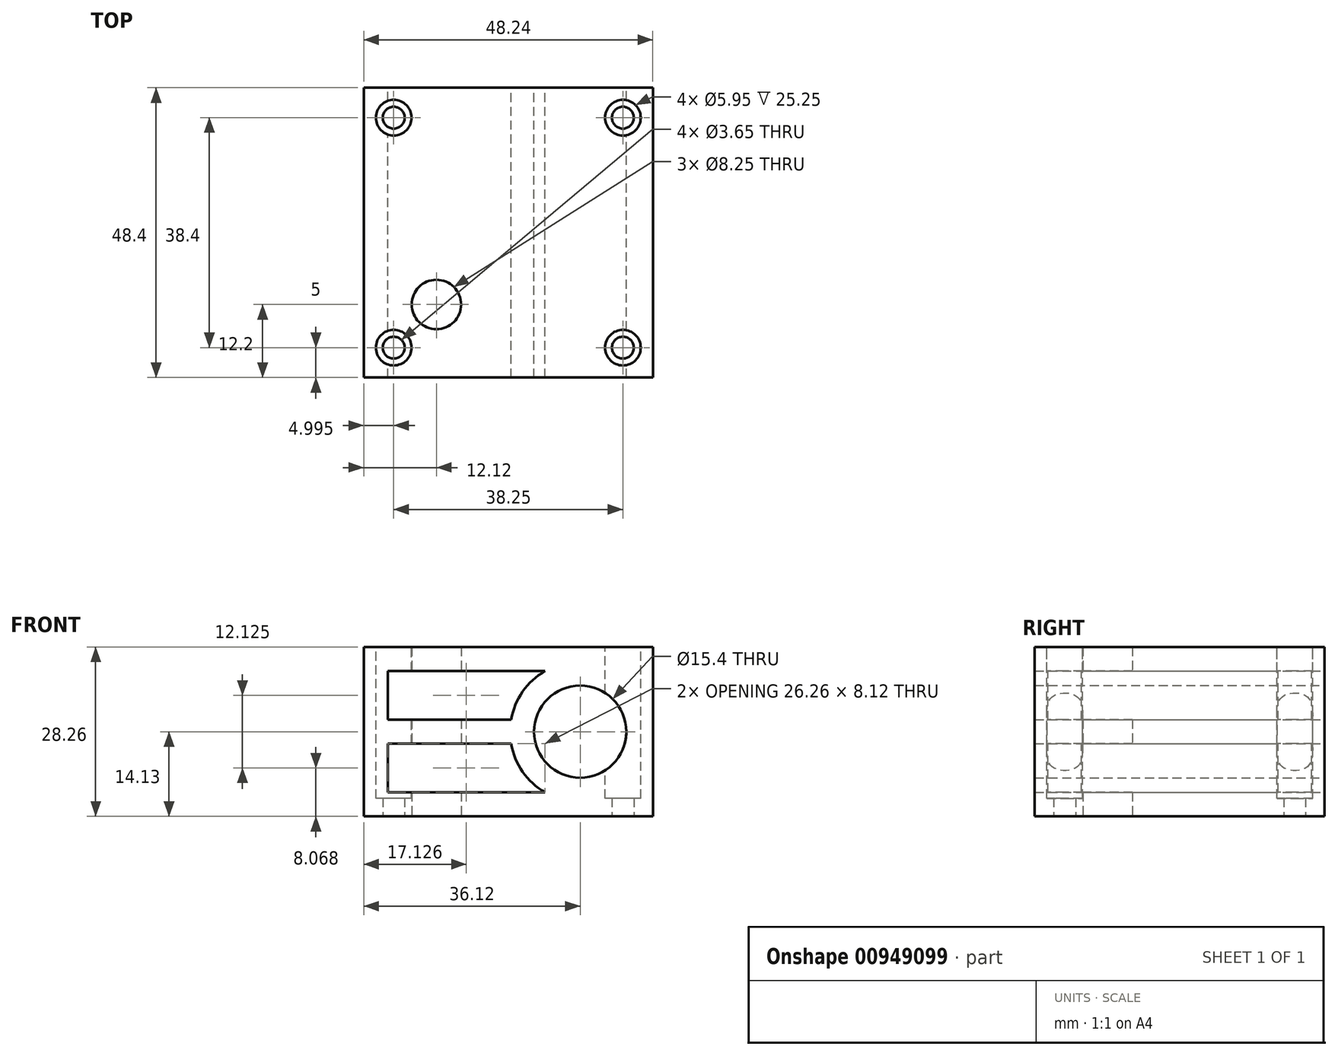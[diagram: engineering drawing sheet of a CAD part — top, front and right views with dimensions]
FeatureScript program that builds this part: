
annotation { "Feature Type Name" : "Feature", "Feature Type Description" : "" }
export const myFeature = defineFeature(function(context is Context, id is Id, definition is map)
    precondition{}
    {
        {
            assignVariable(context, id + "F0", {"name" : "tolerance_xy", "anyValue" : 0.25});
        }
        {
            assignVariable(context, id + "F1", {"name" : "tolerance_z", "anyValue" : 0.4});
        }
        {
            var Q0;
            Q0=qCreatedBy(makeId("Front.planeOp"),FACE);
            var sketch = newSketch(context, id + "F2", { "sketchPlane" : qUnion([Q0])});
            skLineSegment(sketch, "E0.bottom", {"start": v(24.12, 14.12) * mm, "end": v(-24.12, 14.12) * mm});
            skLineSegment(sketch, "E0.top", {"start": v(24.12, -14.12) * mm, "end": v(-24.12, -14.12) * mm});
            skLineSegment(sketch, "E0.left", {"start": v(24.12, 14.12) * mm, "end": v(24.12, -14.12) * mm});
            skLineSegment(sketch, "E0.right", {"start": v(-24.12, 14.12) * mm, "end": v(-24.12, -14.12) * mm});
            skPoint(sketch, "E0.middle", {"position": v(0, 0) * mm});
            skCircle(sketch, "E1", {"center": v(12, 0) * mm, "radius": 11.7 * mm});
            skCircle(sketch, "E2", {"center": v(12, 0) * mm, "radius": 7.7 * mm});
            skLineSegment(sketch, "E3.bottom", {"start": v(20.12, 10.12) * mm, "end": v(-20.12, 10.12) * mm});
            skLineSegment(sketch, "E3.top", {"start": v(20.12, -10.12) * mm, "end": v(-20.12, -10.12) * mm});
            skLineSegment(sketch, "E3.left", {"start": v(20.12, 10.12) * mm, "end": v(20.12, -10.12) * mm});
            skLineSegment(sketch, "E3.right", {"start": v(-20.12, 10.12) * mm, "end": v(-20.12, -10.12) * mm});
            skLineSegment(sketch, "E4", {"start": v(12, -10.12) * mm, "end": v(12, 10.12) * mm, "construction": true});
            skLineSegment(sketch, "E5", {"start": v(-20.12, 0) * mm, "end": v(20.12, 0) * mm, "construction": true});
            skLineSegment(sketch, "E6", {"start": v(0.47, 2) * mm, "end": v(-20.12, 2) * mm});
            skLineSegment(sketch, "E7", {"start": v(0.47, -2) * mm, "end": v(-20.12, -2) * mm});
            skLineSegment(sketch, "E8", {"start": v(10, 10.12) * mm, "end": v(10, 11.53) * mm});
            skLineSegment(sketch, "E9", {"start": v(14, 10.12) * mm, "end": v(14, 11.53) * mm});
            skLineSegment(sketch, "E10", {"start": v(10, -10.12) * mm, "end": v(10, -11.53) * mm});
            skLineSegment(sketch, "E11", {"start": v(14, -10.12) * mm, "end": v(14, -11.53) * mm});
            skLineSegment(sketch, "E12", {"start": v(23.53, 2) * mm, "end": v(20.12, 2) * mm});
            skLineSegment(sketch, "E13", {"start": v(23.53, -2) * mm, "end": v(20.12, -2) * mm});
            skSolve(sketch);
        }
        {
            var Q0;
            Q0=makeQuery(id+"F2.imprint","IMPRINT",FACE,{"disambiguationData":[TD([[makeQuery(id+"F2.imprint","IMPRINT",EDGE,{"derivedFrom":sQuery(id+"F2.wireOp",EDGE,"E0.bottom")}),1.0]])]});
            var Q1;
            {var subQ0=sQuery(id+"F2.wireOp",EDGE,"E8");Q1=makeQuery(id+"F2.imprint","IMPRINT",FACE,{"disambiguationData":[TD([[makeQuery(id+"F2.imprint","IMPRINT",EDGE,{"derivedFrom":subQ0}),-1.0]])]});}
            var Q2;
            Q2=makeQuery(id+"F2.imprint","IMPRINT",FACE,{"disambiguationData":[TD([[makeQuery(id+"F2.imprint","IMPRINT",EDGE,{"derivedFrom":sQuery(id+"F2.wireOp",EDGE,"E2")}),-1.0]])]});
            var Q3;
            {var subQ0=sQuery(id+"F2.wireOp",EDGE,"E10");Q3=makeQuery(id+"F2.imprint","IMPRINT",FACE,{"disambiguationData":[TD([[makeQuery(id+"F2.imprint","IMPRINT",EDGE,{"derivedFrom":subQ0}),1.0]])]});}
            var Q4;
            {var subQ0=sQuery(id+"F2.wireOp",EDGE,"E6");Q4=makeQuery(id+"F2.imprint","IMPRINT",FACE,{"disambiguationData":[TD([[makeQuery(id+"F2.imprint","IMPRINT",EDGE,{"derivedFrom":subQ0}),1.0]])]});}
            var Q5;
            {var subQ0=sQuery(id+"F2.wireOp",EDGE,"E12");Q5=makeQuery(id+"F2.imprint","IMPRINT",FACE,{"disambiguationData":[TD([[makeQuery(id+"F2.imprint","IMPRINT",EDGE,{"derivedFrom":subQ0}),1.0]])]});}
            var Q6;
            {var subQ0=sQuery(id+"F2.wireOp",EDGE,"E12");Q6=makeQuery(id+"F2.imprint","IMPRINT",FACE,{"disambiguationData":[TD([[makeQuery(id+"F2.imprint","IMPRINT",EDGE,{"derivedFrom":subQ0}),-1.0]])]});}
            var Q7;
            {var subQ0=sQuery(id+"F2.wireOp",EDGE,"E13");Q7=makeQuery(id+"F2.imprint","IMPRINT",FACE,{"disambiguationData":[TD([[makeQuery(id+"F2.imprint","IMPRINT",EDGE,{"derivedFrom":subQ0}),1.0]])]});}
            var Q8;
            {var subQ0=sQuery(id+"F2.wireOp",EDGE,"xwtNpsUs-C44z-uagX-IKFE-Rp0NLuXpZdO7");Q8=makeQuery(id+"F2.imprint","IMPRINT",FACE,{"disambiguationData":[TD([[makeQuery(id+"F2.imprint","IMPRINT",EDGE,{"derivedFrom":subQ0}),-1.0]])]});}
            var Q9;
            {var subQ3=sQuery(id+"F2.wireOp",EDGE,"iiPWomU2-JPy6-PKDB-MISC-S4ZnLnR1PTqr");Q9=makeQuery(id+"F2.imprint","IMPRINT",FACE,{"disambiguationData":[TD([[makeQuery(id+"F2.imprint","IMPRINT",EDGE,{"derivedFrom":subQ3}),-1.0]])]});}
            var Q10;
            {var subQ0=sQuery(id+"F2.wireOp",EDGE,"E9");Q10=makeQuery(id+"F2.imprint","IMPRINT",FACE,{"disambiguationData":[TD([[makeQuery(id+"F2.imprint","IMPRINT",EDGE,{"derivedFrom":subQ0}),-1.0]])]});}
            var Q11;
            {var subQ0=sQuery(id+"F2.wireOp",EDGE,"E8");Q11=makeQuery(id+"F2.imprint","IMPRINT",FACE,{"disambiguationData":[TD([[makeQuery(id+"F2.imprint","IMPRINT",EDGE,{"derivedFrom":subQ0}),1.0]])]});}
            var Q12;
            {var subQ0=sQuery(id+"F2.wireOp",EDGE,"E11");Q12=makeQuery(id+"F2.imprint","IMPRINT",FACE,{"disambiguationData":[TD([[makeQuery(id+"F2.imprint","IMPRINT",EDGE,{"derivedFrom":subQ0}),1.0]])]});}
            var Q13;
            {var subQ0=sQuery(id+"F2.wireOp",EDGE,"E10");Q13=makeQuery(id+"F2.imprint","IMPRINT",FACE,{"disambiguationData":[TD([[makeQuery(id+"F2.imprint","IMPRINT",EDGE,{"derivedFrom":subQ0}),-1.0]])]});}
            var Q14;
            {var subQ0=sQuery(id+"F2.wireOp",EDGE,"E3.left");var subQ1=sQuery(id+"F2.wireOp",EDGE,"E1");var subQ2=makeQuery(id+"F2.imprint","INTERSECT",VERTEX,{"disambiguationData":[OD(0.0)],"derivedFrom":[subQ1,subQ0]});Q14=makeQuery(id+"F2.imprint","IMPRINT",FACE,{"disambiguationData":[TD([[makeQuery(id+"F2.imprint","IMPRINT",EDGE,{"disambiguationData":[TD([[subQ2,-1.0]])],"derivedFrom":subQ1}),-1.0]])]});}
            var Q15;
            {var subQ0=sQuery(id+"F2.wireOp",EDGE,"E3.top");var subQ1=sQuery(id+"F2.wireOp",EDGE,"E1");var subQ2=makeQuery(id+"F2.imprint","INTERSECT",VERTEX,{"disambiguationData":[OD(1.0)],"derivedFrom":[subQ1,subQ0]});Q15=makeQuery(id+"F2.imprint","IMPRINT",FACE,{"disambiguationData":[TD([[makeQuery(id+"F2.imprint","IMPRINT",EDGE,{"disambiguationData":[TD([[subQ2,-1.0]])],"derivedFrom":subQ1}),-1.0]])]});}
            extrude(context, id + "F3", {"entities" : qUnion([Q0, Q1, Q2, Q3, Q4, Q5, Q6, Q7, Q8, Q9, Q10, Q11, Q12, Q13, Q14, Q15]), "endBound" : BoundingType.SYMMETRIC, "depth" : (48 + getVariable(context, 'tolerance_z')) * mm, "offsetDistance" : 25 * mm});
        }
        {
            var Q0;
            Q0=makeQuery(id+"F3.opExtrude","SWEPT_FACE",FACE,{"disambiguationData":[OSD([sQuery(id+"F2.wireOp",EDGE,"E0.top")])]});
            var sketch = newSketch(context, id + "F4", { "sketchPlane" : qUnion([Q0])});
            skLineSegment(sketch, "E14.0", {"start": v(24.12, 24.2) * mm, "end": v(-24.12, 24.2) * mm});
            skLineSegment(sketch, "E14.1", {"start": v(-24.12, 24.2) * mm, "end": v(-24.12, -24.2) * mm});
            skLineSegment(sketch, "E14.3", {"start": v(24.12, -24.2) * mm, "end": v(-24.12, -24.2) * mm});
            skLineSegment(sketch, "E14.4", {"start": v(24.12, 24.2) * mm, "end": v(24.12, -24.2) * mm});
            skCircle(sketch, "E15", {"center": v(-19.12, 19.2) * mm, "radius": 1.82 * mm});
            skCircle(sketch, "E16", {"center": v(19.12, 19.2) * mm, "radius": 1.82 * mm});
            skCircle(sketch, "E17", {"center": v(19.12, -19.2) * mm, "radius": 1.82 * mm});
            skCircle(sketch, "E18", {"center": v(-19.12, -19.2) * mm, "radius": 1.82 * mm});
            skLineSegment(sketch, "E19", {"start": v(0, 24.2) * mm, "end": v(0, -24.2) * mm, "construction": true});
            skLineSegment(sketch, "E20", {"start": v(-24.12, 0) * mm, "end": v(24.12, 0) * mm, "construction": true});
            skCircle(sketch, "E21", {"center": v(-12, 12) * mm, "radius": 4.12 * mm});
            skSolve(sketch);
        }
        {
            var Q0;
            Q0=makeQuery(id+"F3.opExtrude","SWEPT_FACE",FACE,{"disambiguationData":[OSD([sQuery(id+"F2.wireOp",EDGE,"E0.bottom")])]});
            var sketch = newSketch(context, id + "F5", { "sketchPlane" : qUnion([Q0])});
            skCircle(sketch, "E22.0.0", {"center": v(-19.12, -19.2) * mm, "radius": 1.83 * mm, "construction": true});
            skCircle(sketch, "E22.1.0", {"center": v(19.12, -19.2) * mm, "radius": 1.83 * mm, "construction": true});
            skCircle(sketch, "E22.2.0", {"center": v(19.12, 19.2) * mm, "radius": 1.83 * mm, "construction": true});
            skCircle(sketch, "E22.3.0", {"center": v(-19.12, 19.2) * mm, "radius": 1.83 * mm, "construction": true});
            skCircle(sketch, "E23", {"center": v(19.12, 19.2) * mm, "radius": 2.98 * mm});
            skCircle(sketch, "E24", {"center": v(19.12, -19.2) * mm, "radius": 2.98 * mm});
            skCircle(sketch, "E25", {"center": v(-19.12, -19.2) * mm, "radius": 2.98 * mm});
            skCircle(sketch, "E26", {"center": v(-19.12, 19.2) * mm, "radius": 2.98 * mm});
            skSolve(sketch);
        }
        {
            var Q0;
            Q0=makeQuery(id+"F5.imprint","IMPRINT",FACE,{"disambiguationData":[TD([[makeQuery(id+"F5.imprint","IMPRINT",EDGE,{"derivedFrom":sQuery(id+"F5.wireOp",EDGE,"E26")}),1.0]])]});
            var Q1;
            Q1=makeQuery(id+"F5.imprint","IMPRINT",FACE,{"disambiguationData":[TD([[makeQuery(id+"F5.imprint","IMPRINT",EDGE,{"derivedFrom":sQuery(id+"F5.wireOp",EDGE,"E24")}),1.0]])]});
            var Q2;
            Q2=makeQuery(id+"F5.imprint","IMPRINT",FACE,{"disambiguationData":[TD([[makeQuery(id+"F5.imprint","IMPRINT",EDGE,{"derivedFrom":sQuery(id+"F5.wireOp",EDGE,"E25")}),1.0]])]});
            var Q3;
            Q3=makeQuery(id+"F5.imprint","IMPRINT",FACE,{"disambiguationData":[TD([[makeQuery(id+"F5.imprint","IMPRINT",EDGE,{"derivedFrom":sQuery(id+"F5.wireOp",EDGE,"E23")}),1.0]])]});
            extrude(context, id + "F6", {"entities" : qUnion([Q0, Q1, Q2, Q3]), "operationType" : NewBodyOperationType.REMOVE, "oppositeDirection" : true, "depth" : (28 - 3 + getVariable(context, 'tolerance_xy')) * mm, "offsetDistance" : 25 * mm});
        }
        {
            var Q0;
            Q0=makeQuery(id+"F4.imprint","IMPRINT",FACE,{"disambiguationData":[TD([[makeQuery(id+"F4.imprint","IMPRINT",EDGE,{"derivedFrom":sQuery(id+"F4.wireOp",EDGE,"E15")}),1.0]])]});
            var Q1;
            Q1=makeQuery(id+"F4.imprint","IMPRINT",FACE,{"disambiguationData":[TD([[makeQuery(id+"F4.imprint","IMPRINT",EDGE,{"derivedFrom":sQuery(id+"F4.wireOp",EDGE,"E16")}),1.0]])]});
            var Q2;
            Q2=makeQuery(id+"F4.imprint","IMPRINT",FACE,{"disambiguationData":[TD([[makeQuery(id+"F4.imprint","IMPRINT",EDGE,{"derivedFrom":sQuery(id+"F4.wireOp",EDGE,"E17")}),1.0]])]});
            var Q3;
            Q3=makeQuery(id+"F4.imprint","IMPRINT",FACE,{"disambiguationData":[TD([[makeQuery(id+"F4.imprint","IMPRINT",EDGE,{"derivedFrom":sQuery(id+"F4.wireOp",EDGE,"E18")}),1.0]])]});
            extrude(context, id + "F7", {"entities" : qUnion([Q0, Q1, Q2, Q3]), "operationType" : NewBodyOperationType.REMOVE, "oppositeDirection" : true, "depth" : (28 + getVariable(context, 'tolerance_xy')) * mm, "offsetDistance" : 25 * mm});
        }
        {
            var Q0;
            Q0=makeQuery(id+"F4.imprint","IMPRINT",FACE,{"disambiguationData":[TD([[makeQuery(id+"F4.imprint","IMPRINT",EDGE,{"derivedFrom":sQuery(id+"F4.wireOp",EDGE,"E21")}),1.0]])]});
            extrude(context, id + "F8", {"entities" : qUnion([Q0]), "operationType" : NewBodyOperationType.REMOVE, "oppositeDirection" : true, "depth" : (28 + getVariable(context, 'tolerance_xy')) * mm, "offsetDistance" : 25 * mm});
        }
    });
